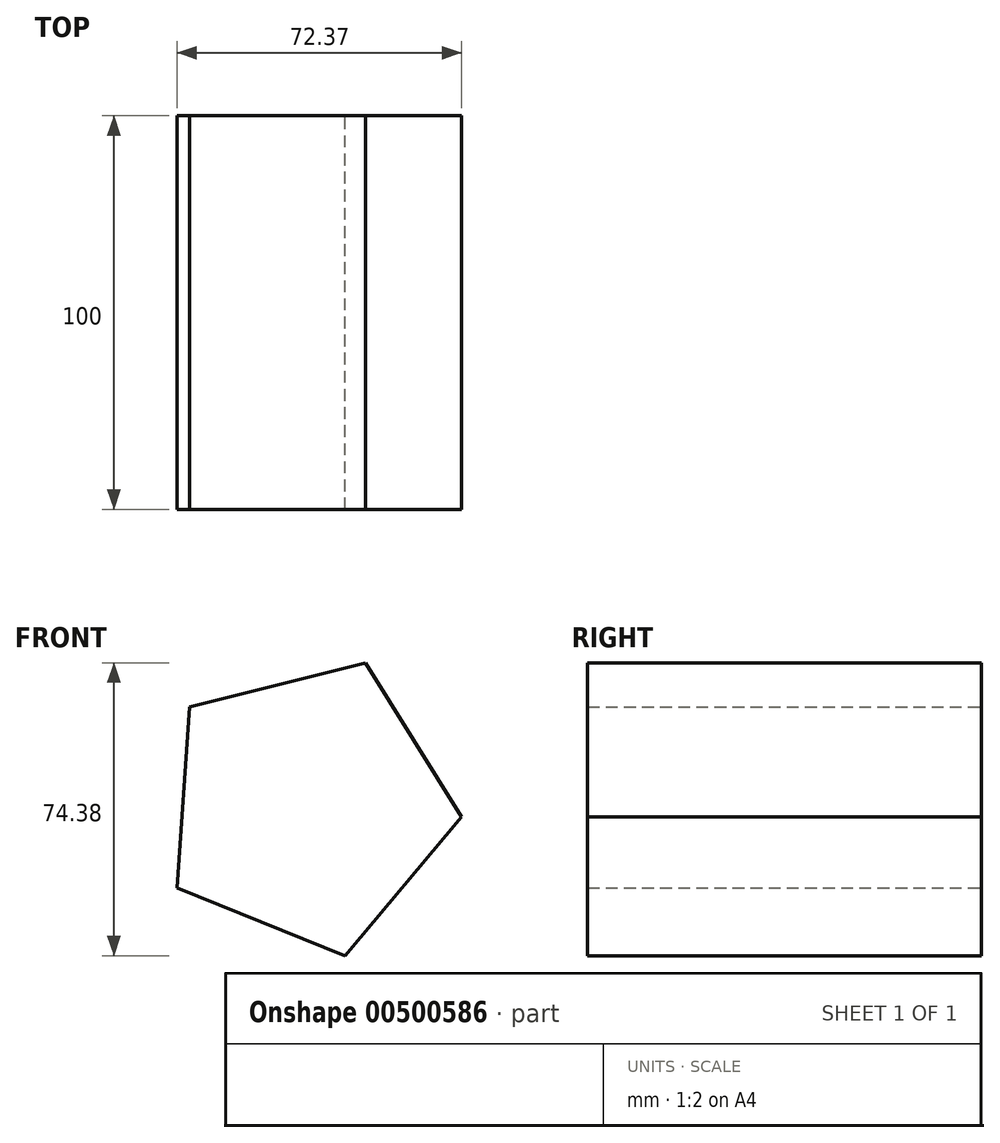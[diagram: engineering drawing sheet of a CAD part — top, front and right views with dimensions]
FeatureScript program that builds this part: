
annotation { "Feature Type Name" : "Feature", "Feature Type Description" : "" }
export const myFeature = defineFeature(function(context is Context, id is Id, definition is map)
    precondition{}
    {
        {
            var Q0;
            Q0=qCreatedBy(makeId("Front.planeOp"),FACE);
            var sketch = newSketch(context, id + "F0", { "sketchPlane" : qUnion([Q0])});
            skCircle(sketch, "E0.cCircle", {"center": v(0, 0) * mm, "radius": 39.2 * mm, "construction": true});
            skLineSegment(sketch, "E0.0", {"start": v(-30.02, 25.21) * mm, "end": v(14.7, 36.34) * mm});
            skLineSegment(sketch, "E0.1", {"start": v(14.7, 36.34) * mm, "end": v(39.1, -2.75) * mm});
            skLineSegment(sketch, "E0.2", {"start": v(39.1, -2.75) * mm, "end": v(9.47, -38.04) * mm});
            skLineSegment(sketch, "E0.3", {"start": v(9.47, -38.04) * mm, "end": v(-33.26, -20.76) * mm});
            skLineSegment(sketch, "E0.4", {"start": v(-33.26, -20.76) * mm, "end": v(-30.02, 25.21) * mm});
            skSolve(sketch);
        }
        {
            var Q0;
            Q0=makeQuery(id+"F0.imprint","IMPRINT",FACE,{"disambiguationData":[TD([[makeQuery(id+"F0.imprint","IMPRINT",EDGE,{"derivedFrom":sQuery(id+"F0.wireOp",EDGE,"E0.0")}),-1.0]])]});
            extrude(context, id + "F1", {"entities" : qUnion([Q0]), "endBound" : BoundingType.SYMMETRIC, "depth" : 100 * mm});
        }
    });
